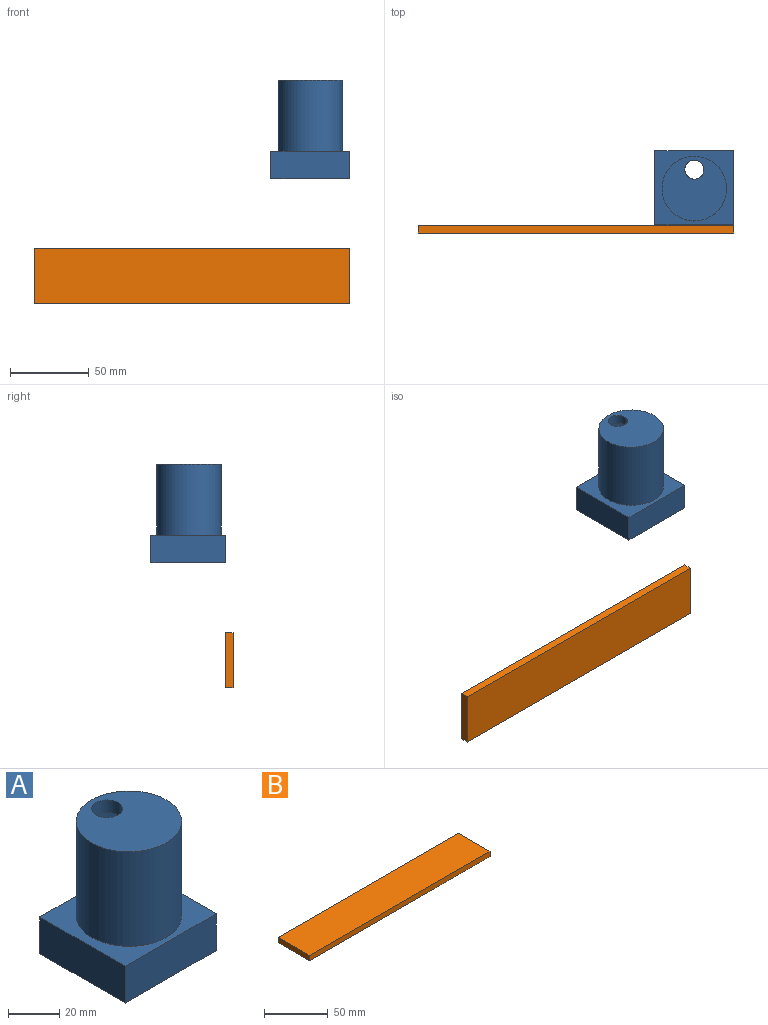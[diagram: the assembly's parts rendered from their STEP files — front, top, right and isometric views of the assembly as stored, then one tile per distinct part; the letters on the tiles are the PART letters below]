
ASSEMBLY  parts=2 mates=2
PART A: 11 faces, bbox 50x47x62.5 mm
  f0: plane 50x17.5mm, normal (0,1,0), area 875mm2, adj f1,f3,f4,f5
  f1: plane 47x17.5mm, normal (-1,0,0), area 822.5mm2, adj f0,f2,f4,f5
  f2: plane 50x17.5mm, normal (0,-1,0), area 875mm2, adj f1,f3,f4,f5
  f3: plane 47x17.5mm, normal (1,0,0), area 822.5mm2, adj f0,f2,f4,f5
  f4: plane 50x47mm, normal (0,0,1), area 1029.7mm2, adj f0,f1,f2,f3,f6
  f5: plane 50x47mm, normal (0,0,-1), area 1274.8mm2, adj f0,f1,f2,f3,f8
  f6: cylinder r=20.5mm len=45mm, axis (0,0,-1), area 5796.2mm2, adj f4,f7
  f7: plane 41x41mm, normal (0,0,1), area 1207.2mm2, adj f6,f10
  f8: cylinder r=18.5mm len=56.5mm, axis (0,0,-1), area 6567.5mm2, adj f5,f9
  f9: plane 37x37mm, normal (0,0,-1), area 962.1mm2, adj f8,f10
  f10: cylinder r=6mm len=12mm, axis (0,0,1), area 226.2mm2, adj f7,f9
PART B: 6 faces, bbox 200x35x5 mm
  f0: plane 35x5mm, normal (-1,0,0), area 175mm2, adj f1,f3,f4,f5
  f1: plane 200x5mm, normal (0,-1,0), area 1000mm2, adj f0,f2,f4,f5
  f2: plane 35x5mm, normal (1,0,0), area 175mm2, adj f1,f3,f4,f5
  f3: plane 200x5mm, normal (0,1,0), area 1000mm2, adj f0,f2,f4,f5
  f4: plane 200x35mm, normal (0,0,1), area 7000mm2, adj f0,f1,f2,f3
  f5: plane 200x35mm, normal (0,0,-1), area 7000mm2, adj f0,f1,f2,f3
PLACE A at identity fixed
PLACE B rot(axis=(-1,0,0),90deg) t=(-150,-5,-44.34)mm
MATE planar B.f4 <-> A.f2  axis (0,1,0) through (-50,0,-61.84)mm
MATE planar A.f3 <-> B.f2  axis (1,0,0) through (50,23.5,8.75)mm
